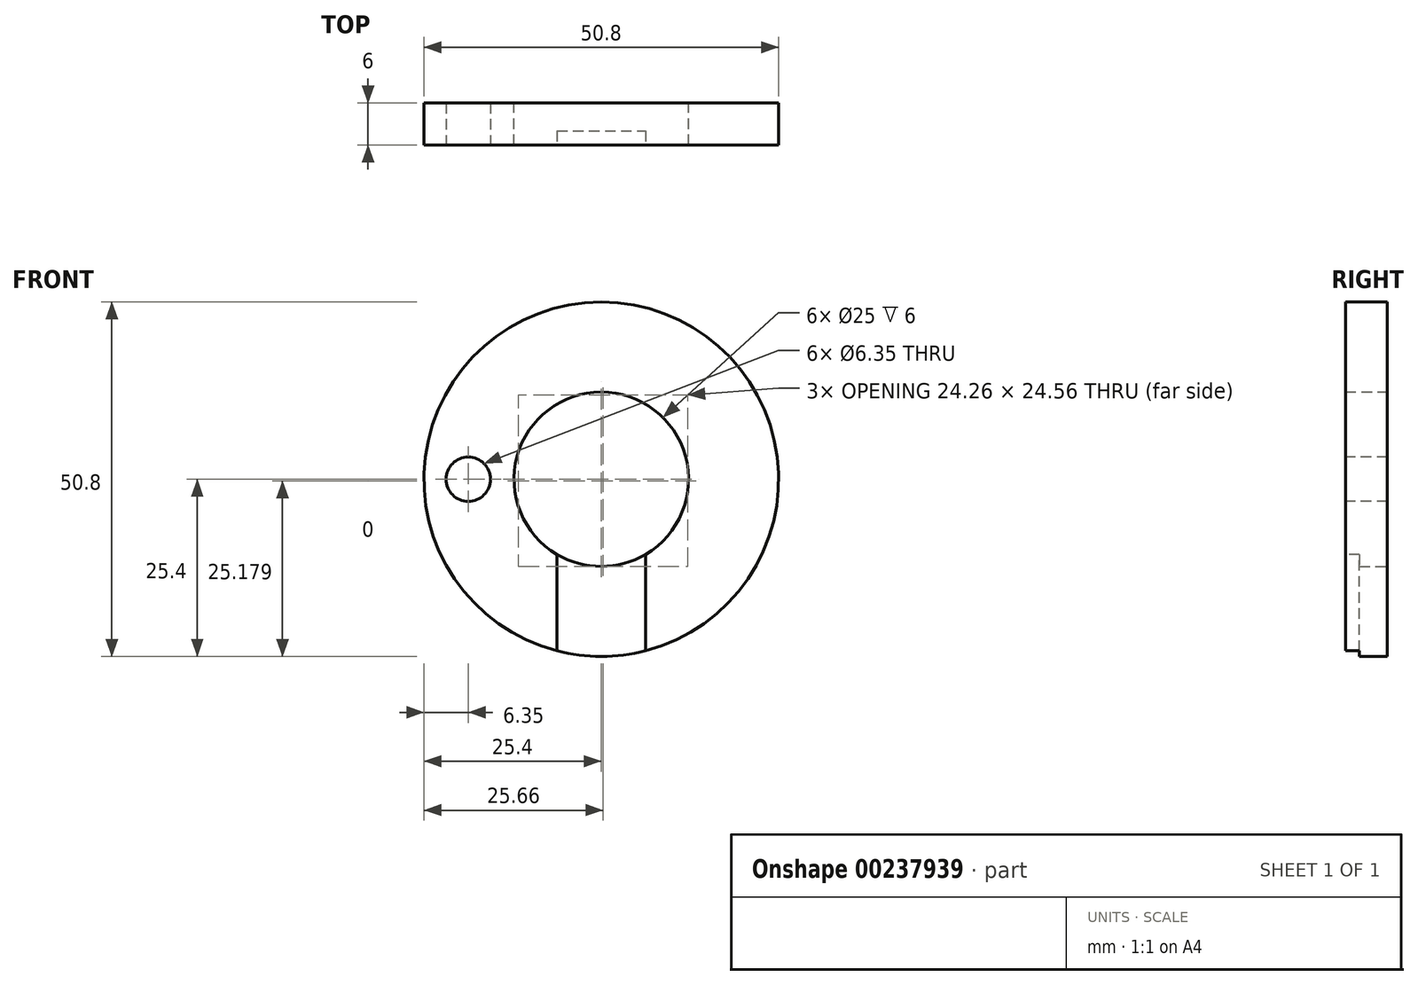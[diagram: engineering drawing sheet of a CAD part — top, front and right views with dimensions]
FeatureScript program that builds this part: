
annotation { "Feature Type Name" : "Feature", "Feature Type Description" : "" }
export const myFeature = defineFeature(function(context is Context, id is Id, definition is map)
    precondition{}
    {
        {
            var Q0;
            Q0=qCreatedBy(makeId("Front.planeOp"),FACE);
            var sketch = newSketch(context, id + "F0", { "sketchPlane" : qUnion([Q0])});
            skCircle(sketch, "E0", {"center": v(0, 0) * mm, "radius": 25.4 * mm});
            skCircle(sketch, "E1", {"center": v(0, 0) * mm, "radius": 12.5 * mm});
            skSolve(sketch);
        }
        {
            var Q0;
            Q0=makeQuery(id+"F0.imprint","IMPRINT",FACE,{"disambiguationData":[TD([[makeQuery(id+"F0.imprint","IMPRINT",EDGE,{"derivedFrom":sQuery(id+"F0.wireOp",EDGE,"E0")}),1.0]])]});
            extrude(context, id + "F1", {"entities" : qUnion([Q0]), "depth" : 6 * mm});
        }
        {
            var Q0;
            Q0=makeQuery(id+"F1.opExtrude","CAP_FACE",FACE,{"disambiguationData":[OSD([sQuery(id+"F0.wireOp",EDGE,"E0"),sQuery(id+"F0.wireOp",EDGE,"E1")])],"isStart":false});
            var sketch = newSketch(context, id + "F2", { "sketchPlane" : qUnion([Q0])});
            skLineSegment(sketch, "E2.bottom", {"start": v(6.35, -36.17) * mm, "end": v(-6.35, -36.17) * mm});
            skLineSegment(sketch, "E2.top", {"start": v(6.35, -10.77) * mm, "end": v(-6.35, -10.77) * mm});
            skLineSegment(sketch, "E2.left", {"start": v(6.35, -36.17) * mm, "end": v(6.35, -10.77) * mm});
            skLineSegment(sketch, "E2.right", {"start": v(-6.35, -36.17) * mm, "end": v(-6.35, -10.77) * mm});
            skPoint(sketch, "E2.middle", {"position": v(0, -23.47) * mm});
            skSolve(sketch);
        }
        {
            var Q0;
            {var subQ0=sQuery(id+"F2.wireOp",EDGE,"E2.left");var subQ4=makeQuery(id+"F1.opExtrude","CAP_EDGE",EDGE,{"disambiguationData":[OSD([sQuery(id+"F0.wireOp",EDGE,"E0")])],"isStart":false});var subQ5=makeQuery(id+"F2.imprint","INTERSECT",VERTEX,{"derivedFrom":[subQ4,subQ0]});Q0=makeQuery(id+"F2.imprint","IMPRINT",FACE,{"disambiguationData":[TD([[makeQuery(id+"F2.imprint","IMPRINT",EDGE,{"disambiguationData":[TD([[subQ5,1.0]])],"derivedFrom":subQ4}),1.0]])]});}
            extrude(context, id + "F3", {"entities" : qUnion([Q0]), "operationType" : NewBodyOperationType.REMOVE, "oppositeDirection" : true, "depth" : 2 * mm});
        }
        {
            var Q0;
            Q0=makeQuery(id+"F1.opExtrude","CAP_FACE",FACE,{"disambiguationData":[OSD([sQuery(id+"F0.wireOp",EDGE,"E0"),sQuery(id+"F0.wireOp",EDGE,"E1")])],"isStart":false});
            var sketch = newSketch(context, id + "F4", { "sketchPlane" : qUnion([Q0])});
            skCircle(sketch, "E3", {"center": v(-19.05, 0) * mm, "radius": 3.18 * mm});
            skSolve(sketch);
        }
        {
            var Q0;
            Q0=makeQuery(id+"F4.imprint","IMPRINT",FACE,{"disambiguationData":[TD([[makeQuery(id+"F4.imprint","IMPRINT",EDGE,{"derivedFrom":sQuery(id+"F4.wireOp",EDGE,"E3")}),1.0]])]});
            extrude(context, id + "F5", {"entities" : qUnion([Q0]), "operationType" : NewBodyOperationType.REMOVE, "endBound" : BoundingType.THROUGH_ALL, "oppositeDirection" : true, "depth" : 25.4 * mm});
        }
    });
